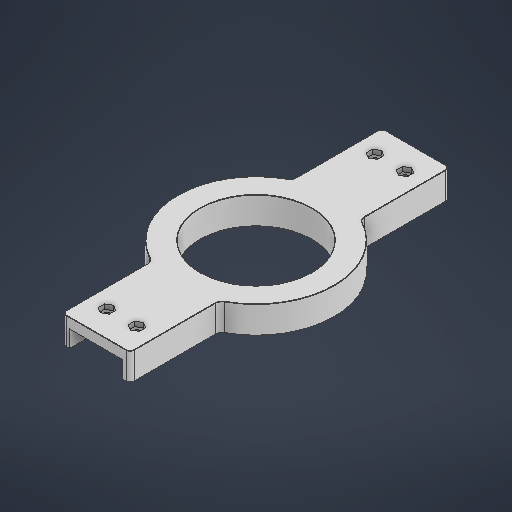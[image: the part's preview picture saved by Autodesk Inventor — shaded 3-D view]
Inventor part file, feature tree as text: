
AUTODESK INVENTOR PART (.ipt)
format: ipt  version: 2025 (Build 290162000, 162)  size: 389,632 bytes
history: native  units: in
note: dims shown in document units (in); Inventor stores cm internally (conversion verified against a paired STEP export)
features: sketch x6, extrude x4, fillet x2, chamfer x1, hole x1
ambient origin geometry x8: Origin, YZ Plane, XZ Plane, XY Plane, X Axis, Y Axis, Z Axis, Center Point
bodies: Solid1 (feature_tree)
feature tree (14):
  extrude  "Extrusion1"  Depth=0.1969in
  fillet  "Fillet1"  Radius=0.7874in
  fillet  "Fillet2"  Radius=0.1969in
  chamfer  "Chamfer1"  Distance=0.0098in Angle=45.0deg
  extrude  "Extrusion4"  Depth=1.5453in
  hole  "Hole2"  [1 undecoded]
  extrude  "Extrusion5"  Depth=0.1181in
  extrude  "Extrusion6"  Depth=0.4951in TaperAngle=0.0deg
  sketch  "Sketch1"  dims[d0=3.2283in d3=4.5276in d4=0.7874in d5=0.0in d28=0.1969in]
  sketch  "Sketch3"  dims[d29=0.1181in d30=0.0098in d31=0.0787in d32=45.0deg]
  sketch  "Sketch4"  dims[d38=1.1122in d39=1.5453in]
  sketch  "Sketch5"  dims[d40=0.1181in d41=0.1181in]
  sketch  "Sketch6"  dims[d42=0.1181in d43=0.4951in d44=0.0in d45=0.748in d48=0.748in d50=0.0935in d51=0.0935in d52=1.7323in d53=1.5453in d55=0.0935in d56=0.0935in d57=0.748in d58=0.748in d59=0.8661in d60=0.8661in d61=0.3396in d62=0.3396in d63=0.1628in d64=0.3937in d65=0.1575in d66=0.0787in d67=90.0deg d68=0.315in d69=0.8108in d70=0.3248in d71=0.3248in d72=0.3248in d73=0.3248in d74=0.1358in d75=0.0in d76=1.9685in d77=2.2638in d78=2.2638in d79=2.5874in d80=2.5874in d81=1.9685in d82=9.252in d83=9.2323in d84=3.7402in d85=0.2756in d86=3.1496in d88=360.0deg d90=0.2756in d91=0.0in d92=0.1768in d46=0.0344in]
  sketch  "Sketch Circular Pattern3"  dims[d35=1.5453in d37=1.1122in]
note: 1 required parameter value undecoded (feature->parameter linkage not recoverable at this tier; creation-order binding heuristic only, values carry confidence <= 0.55)
